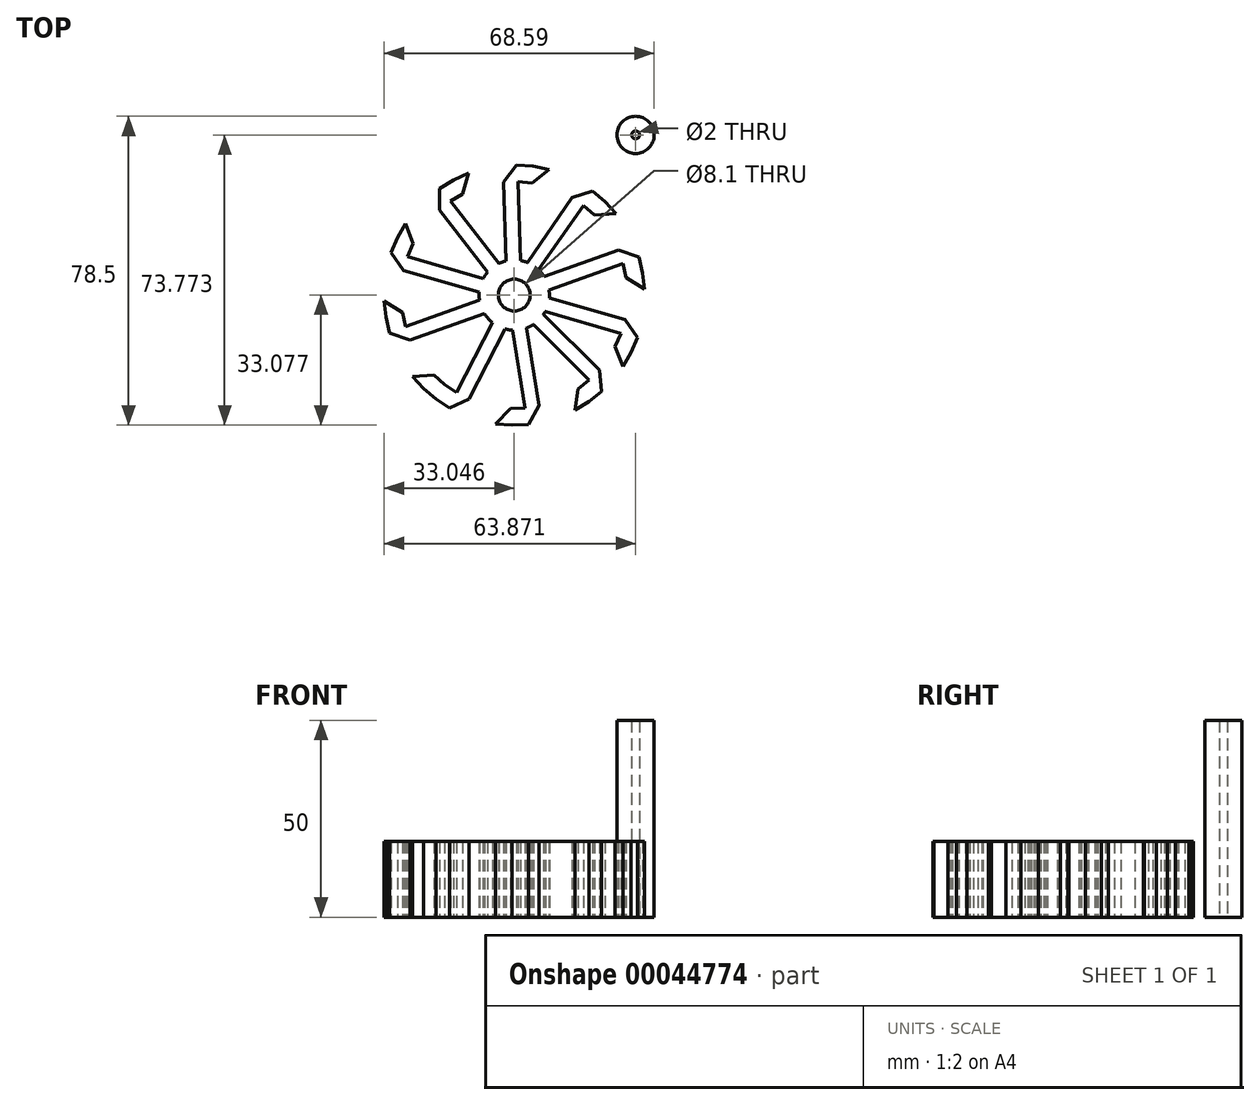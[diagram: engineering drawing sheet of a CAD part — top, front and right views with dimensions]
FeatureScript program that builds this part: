
annotation { "Feature Type Name" : "Feature", "Feature Type Description" : "" }
export const myFeature = defineFeature(function(context is Context, id is Id, definition is map)
    precondition{}
    {
        {
            var Q0;
            Q0=qCreatedBy(makeId("Top.planeOp"),FACE);
            var sketch = newSketch(context, id + "F0", { "sketchPlane" : qUnion([Q0])});
            skCircle(sketch, "E0.cCircle", {"center": v(0.32, -0.47) * mm, "radius": 28.74 * mm, "construction": true});
            skLineSegment(sketch, "E0.0", {"start": v(-15.87, 23.34) * mm, "end": v(-12.76, 25.18) * mm});
            skLineSegment(sketch, "E0.1", {"start": v(-12.76, 25.18) * mm, "end": v(-9.44, 26.62) * mm});
            skLineSegment(sketch, "E0.2", {"start": v(-9.44, 26.62) * mm, "end": v(-5.96, 27.63) * mm});
            skLineSegment(sketch, "E0.3", {"start": v(-5.96, 27.63) * mm, "end": v(-2.4, 28.2) * mm});
            skLineSegment(sketch, "E0.4", {"start": v(-2.4, 28.2) * mm, "end": v(1.22, 28.3) * mm});
            skLineSegment(sketch, "E0.5", {"start": v(1.22, 28.3) * mm, "end": v(4.82, 27.97) * mm});
            skLineSegment(sketch, "E0.6", {"start": v(4.82, 27.97) * mm, "end": v(8.35, 27.18) * mm});
            skLineSegment(sketch, "E0.7", {"start": v(8.35, 27.18) * mm, "end": v(11.75, 25.95) * mm});
            skLineSegment(sketch, "E0.8", {"start": v(11.75, 25.95) * mm, "end": v(14.98, 24.31) * mm});
            skLineSegment(sketch, "E0.9", {"start": v(14.98, 24.31) * mm, "end": v(17.97, 22.28) * mm});
            skLineSegment(sketch, "E0.10", {"start": v(17.97, 22.28) * mm, "end": v(20.68, 19.89) * mm});
            skLineSegment(sketch, "E0.11", {"start": v(20.68, 19.89) * mm, "end": v(23.07, 17.17) * mm});
            skLineSegment(sketch, "E0.12", {"start": v(23.07, 17.17) * mm, "end": v(25.1, 14.18) * mm});
            skLineSegment(sketch, "E0.13", {"start": v(25.1, 14.18) * mm, "end": v(26.74, 10.96) * mm});
            skLineSegment(sketch, "E0.14", {"start": v(26.74, 10.96) * mm, "end": v(27.97, 7.56) * mm});
            skLineSegment(sketch, "E0.15", {"start": v(27.97, 7.56) * mm, "end": v(28.76, 4.03) * mm});
            skLineSegment(sketch, "E0.16", {"start": v(28.76, 4.03) * mm, "end": v(29.1, 0.43) * mm});
            skLineSegment(sketch, "E0.17", {"start": v(29.1, 0.43) * mm, "end": v(28.98, -3.19) * mm});
            skLineSegment(sketch, "E0.18", {"start": v(28.98, -3.19) * mm, "end": v(28.42, -6.76) * mm});
            skLineSegment(sketch, "E0.19", {"start": v(28.42, -6.76) * mm, "end": v(27.4, -10.23) * mm});
            skLineSegment(sketch, "E0.20", {"start": v(27.4, -10.23) * mm, "end": v(25.97, -13.55) * mm});
            skLineSegment(sketch, "E0.21", {"start": v(25.97, -13.55) * mm, "end": v(24.13, -16.66) * mm});
            skLineSegment(sketch, "E0.22", {"start": v(24.13, -16.66) * mm, "end": v(21.91, -19.52) * mm});
            skLineSegment(sketch, "E0.23", {"start": v(21.91, -19.52) * mm, "end": v(19.36, -22.07) * mm});
            skLineSegment(sketch, "E0.24", {"start": v(19.36, -22.07) * mm, "end": v(16.5, -24.3) * mm});
            skLineSegment(sketch, "E0.25", {"start": v(16.5, -24.3) * mm, "end": v(13.39, -26.13) * mm});
            skLineSegment(sketch, "E0.26", {"start": v(13.39, -26.13) * mm, "end": v(10.07, -27.57) * mm});
            skLineSegment(sketch, "E0.27", {"start": v(10.07, -27.57) * mm, "end": v(6.6, -28.58) * mm});
            skLineSegment(sketch, "E0.28", {"start": v(6.6, -28.58) * mm, "end": v(3.02, -29.14) * mm});
            skLineSegment(sketch, "E0.29", {"start": v(3.02, -29.14) * mm, "end": v(-0.6, -29.25) * mm});
            skLineSegment(sketch, "E0.30", {"start": v(-0.6, -29.25) * mm, "end": v(-4.2, -28.91) * mm});
            skLineSegment(sketch, "E0.31", {"start": v(-4.2, -28.91) * mm, "end": v(-7.72, -28.13) * mm});
            skLineSegment(sketch, "E0.32", {"start": v(-7.72, -28.13) * mm, "end": v(-11.12, -26.9) * mm});
            skLineSegment(sketch, "E0.33", {"start": v(-11.12, -26.9) * mm, "end": v(-14.34, -25.26) * mm});
            skLineSegment(sketch, "E0.34", {"start": v(-14.34, -25.26) * mm, "end": v(-17.33, -23.23) * mm});
            skLineSegment(sketch, "E0.35", {"start": v(-17.33, -23.23) * mm, "end": v(-20.05, -20.83) * mm});
            skLineSegment(sketch, "E0.36", {"start": v(-20.05, -20.83) * mm, "end": v(-22.44, -18.12) * mm});
            skLineSegment(sketch, "E0.37", {"start": v(-22.44, -18.12) * mm, "end": v(-24.47, -15.13) * mm});
            skLineSegment(sketch, "E0.38", {"start": v(-24.47, -15.13) * mm, "end": v(-26.11, -11.9) * mm});
            skLineSegment(sketch, "E0.39", {"start": v(-26.11, -11.9) * mm, "end": v(-27.34, -8.5) * mm});
            skLineSegment(sketch, "E0.40", {"start": v(-27.34, -8.5) * mm, "end": v(-28.13, -4.98) * mm});
            skLineSegment(sketch, "E0.41", {"start": v(-28.13, -4.98) * mm, "end": v(-28.47, -1.38) * mm});
            skLineSegment(sketch, "E0.42", {"start": v(-28.47, -1.38) * mm, "end": v(-28.35, 2.24) * mm});
            skLineSegment(sketch, "E0.43", {"start": v(-28.35, 2.24) * mm, "end": v(-27.79, 5.81) * mm});
            skLineSegment(sketch, "E0.44", {"start": v(-27.79, 5.81) * mm, "end": v(-26.78, 9.28) * mm});
            skLineSegment(sketch, "E0.45", {"start": v(-26.78, 9.28) * mm, "end": v(-25.34, 12.6) * mm});
            skLineSegment(sketch, "E0.46", {"start": v(-25.34, 12.6) * mm, "end": v(-23.5, 15.71) * mm});
            skLineSegment(sketch, "E0.47", {"start": v(-23.5, 15.71) * mm, "end": v(-21.28, 18.57) * mm});
            skLineSegment(sketch, "E0.48", {"start": v(-21.28, 18.57) * mm, "end": v(-18.73, 21.13) * mm});
            skLineSegment(sketch, "E0.49", {"start": v(-18.73, 21.13) * mm, "end": v(-15.87, 23.34) * mm});
            skPoint(sketch, "E0.0.midPoint", {"position": v(-14.31, 24.26) * mm});
            skCircle(sketch, "E1.cCircle", {"center": v(0.32, -0.47) * mm, "radius": 33.02 * mm, "construction": true});
            skLineSegment(sketch, "E1.0", {"start": v(-18.67, 26.62) * mm, "end": v(-15.12, 28.79) * mm});
            skLineSegment(sketch, "E1.1", {"start": v(-15.12, 28.79) * mm, "end": v(-11.33, 30.5) * mm});
            skLineSegment(sketch, "E1.2", {"start": v(-11.33, 30.5) * mm, "end": v(-7.36, 31.7) * mm});
            skLineSegment(sketch, "E1.3", {"start": v(-7.36, 31.7) * mm, "end": v(-3.26, 32.42) * mm});
            skLineSegment(sketch, "E1.4", {"start": v(-3.26, 32.42) * mm, "end": v(0.89, 32.6) * mm});
            skLineSegment(sketch, "E1.5", {"start": v(0.89, 32.6) * mm, "end": v(5.03, 32.27) * mm});
            skLineSegment(sketch, "E1.6", {"start": v(5.03, 32.27) * mm, "end": v(9.1, 31.42) * mm});
            skLineSegment(sketch, "E1.7", {"start": v(9.1, 31.42) * mm, "end": v(13.02, 30.07) * mm});
            skLineSegment(sketch, "E1.8", {"start": v(13.02, 30.07) * mm, "end": v(16.75, 28.24) * mm});
            skLineSegment(sketch, "E1.9", {"start": v(16.75, 28.24) * mm, "end": v(20.22, 25.95) * mm});
            skLineSegment(sketch, "E1.10", {"start": v(20.22, 25.95) * mm, "end": v(23.38, 23.25) * mm});
            skLineSegment(sketch, "E1.11", {"start": v(23.38, 23.25) * mm, "end": v(26.17, 20.17) * mm});
            skLineSegment(sketch, "E1.12", {"start": v(26.17, 20.17) * mm, "end": v(28.55, 16.77) * mm});
            skLineSegment(sketch, "E1.13", {"start": v(28.55, 16.77) * mm, "end": v(30.49, 13.1) * mm});
            skLineSegment(sketch, "E1.14", {"start": v(30.49, 13.1) * mm, "end": v(31.95, 9.2) * mm});
            skLineSegment(sketch, "E1.15", {"start": v(31.95, 9.2) * mm, "end": v(32.92, 5.16) * mm});
            skLineSegment(sketch, "E1.16", {"start": v(32.92, 5.16) * mm, "end": v(33.37, 1.03) * mm});
            skLineSegment(sketch, "E1.17", {"start": v(33.37, 1.03) * mm, "end": v(33.3, -3.12) * mm});
            skLineSegment(sketch, "E1.18", {"start": v(33.3, -3.12) * mm, "end": v(32.7, -7.23) * mm});
            skLineSegment(sketch, "E1.19", {"start": v(32.7, -7.23) * mm, "end": v(31.6, -11.24) * mm});
            skLineSegment(sketch, "E1.20", {"start": v(31.6, -11.24) * mm, "end": v(30, -15.07) * mm});
            skLineSegment(sketch, "E1.21", {"start": v(30, -15.07) * mm, "end": v(27.94, -18.68) * mm});
            skLineSegment(sketch, "E1.22", {"start": v(27.94, -18.68) * mm, "end": v(25.44, -22) * mm});
            skLineSegment(sketch, "E1.23", {"start": v(25.44, -22) * mm, "end": v(22.54, -24.98) * mm});
            skLineSegment(sketch, "E1.24", {"start": v(22.54, -24.98) * mm, "end": v(19.3, -27.57) * mm});
            skLineSegment(sketch, "E1.25", {"start": v(19.3, -27.57) * mm, "end": v(15.75, -29.74) * mm});
            skLineSegment(sketch, "E1.26", {"start": v(15.75, -29.74) * mm, "end": v(11.96, -31.44) * mm});
            skLineSegment(sketch, "E1.27", {"start": v(11.96, -31.44) * mm, "end": v(7.99, -32.65) * mm});
            skLineSegment(sketch, "E1.28", {"start": v(7.99, -32.65) * mm, "end": v(3.9, -33.36) * mm});
            skLineSegment(sketch, "E1.29", {"start": v(3.9, -33.36) * mm, "end": v(-0.25, -33.55) * mm});
            skLineSegment(sketch, "E1.30", {"start": v(-0.25, -33.55) * mm, "end": v(-4.4, -33.22) * mm});
            skLineSegment(sketch, "E1.31", {"start": v(-4.4, -33.22) * mm, "end": v(-8.46, -32.37) * mm});
            skLineSegment(sketch, "E1.32", {"start": v(-8.46, -32.37) * mm, "end": v(-12.4, -31.02) * mm});
            skLineSegment(sketch, "E1.33", {"start": v(-12.4, -31.02) * mm, "end": v(-16.12, -29.19) * mm});
            skLineSegment(sketch, "E1.34", {"start": v(-16.12, -29.19) * mm, "end": v(-19.59, -26.9) * mm});
            skLineSegment(sketch, "E1.35", {"start": v(-19.59, -26.9) * mm, "end": v(-22.74, -24.2) * mm});
            skLineSegment(sketch, "E1.36", {"start": v(-22.74, -24.2) * mm, "end": v(-25.54, -21.12) * mm});
            skLineSegment(sketch, "E1.37", {"start": v(-25.54, -21.12) * mm, "end": v(-27.92, -17.72) * mm});
            skLineSegment(sketch, "E1.38", {"start": v(-27.92, -17.72) * mm, "end": v(-29.86, -14.04) * mm});
            skLineSegment(sketch, "E1.39", {"start": v(-29.86, -14.04) * mm, "end": v(-31.32, -10.15) * mm});
            skLineSegment(sketch, "E1.40", {"start": v(-31.32, -10.15) * mm, "end": v(-32.28, -6.11) * mm});
            skLineSegment(sketch, "E1.41", {"start": v(-32.28, -6.11) * mm, "end": v(-32.73, -1.98) * mm});
            skLineSegment(sketch, "E1.42", {"start": v(-32.73, -1.98) * mm, "end": v(-32.66, 2.17) * mm});
            skLineSegment(sketch, "E1.43", {"start": v(-32.66, 2.17) * mm, "end": v(-32.07, 6.29) * mm});
            skLineSegment(sketch, "E1.44", {"start": v(-32.07, 6.29) * mm, "end": v(-30.97, 10.3) * mm});
            skLineSegment(sketch, "E1.45", {"start": v(-30.97, 10.3) * mm, "end": v(-29.37, 14.13) * mm});
            skLineSegment(sketch, "E1.46", {"start": v(-29.37, 14.13) * mm, "end": v(-27.3, 17.73) * mm});
            skLineSegment(sketch, "E1.47", {"start": v(-27.3, 17.73) * mm, "end": v(-24.8, 21.05) * mm});
            skLineSegment(sketch, "E1.48", {"start": v(-24.8, 21.05) * mm, "end": v(-21.91, 24.03) * mm});
            skLineSegment(sketch, "E1.49", {"start": v(-21.91, 24.03) * mm, "end": v(-18.67, 26.62) * mm});
            skPoint(sketch, "E1.0.midPoint", {"position": v(-16.9, 27.7) * mm});
            skCircle(sketch, "E2", {"center": v(0.32, -0.47) * mm, "radius": 8.92 * mm});
            skCircle(sketch, "E3", {"center": v(0.32, -0.47) * mm, "radius": 4.72 * mm});
            skLineSegment(sketch, "E4", {"start": v(0.89, 32.6) * mm, "end": v(-2.4, 28.2) * mm});
            skLineSegment(sketch, "E5", {"start": v(9.1, 31.42) * mm, "end": v(4.82, 27.97) * mm});
            skLineSegment(sketch, "E6", {"start": v(14.98, 24.31) * mm, "end": v(20.22, 25.95) * mm});
            skLineSegment(sketch, "E7", {"start": v(26.17, 20.17) * mm, "end": v(20.68, 19.89) * mm});
            skLineSegment(sketch, "E8", {"start": v(26.74, 10.96) * mm, "end": v(31.95, 9.2) * mm});
            skLineSegment(sketch, "E9", {"start": v(33.37, 1.03) * mm, "end": v(28.76, 4.03) * mm});
            skLineSegment(sketch, "E10", {"start": v(14.98, 24.31) * mm, "end": v(3.73, 7.77) * mm});
            skLineSegment(sketch, "E11", {"start": v(17.97, 22.3) * mm, "end": v(6.5, 5.96) * mm});
            skLineSegment(sketch, "E12", {"start": v(-2.4, 28.2) * mm, "end": v(-1.77, 8.2) * mm});
            skLineSegment(sketch, "E13", {"start": v(1.22, 28.3) * mm, "end": v(1.85, 8.32) * mm});
            skLineSegment(sketch, "E14", {"start": v(26.74, 10.96) * mm, "end": v(7.93, 4.19) * mm});
            skLineSegment(sketch, "E15", {"start": v(27.97, 7.56) * mm, "end": v(9.15, 0.78) * mm});
            skLineSegment(sketch, "E16", {"start": v(28.42, -6.76) * mm, "end": v(31.6, -11.24) * mm});
            skLineSegment(sketch, "E17", {"start": v(27.94, -18.68) * mm, "end": v(25.97, -13.55) * mm});
            skLineSegment(sketch, "E18", {"start": v(28.42, -6.76) * mm, "end": v(9.21, -1.18) * mm});
            skLineSegment(sketch, "E19", {"start": v(27.4, -10.23) * mm, "end": v(8.2, -4.65) * mm});
            skLineSegment(sketch, "E20", {"start": v(21.91, -19.52) * mm, "end": v(7.77, -5.37) * mm});
            skLineSegment(sketch, "E21", {"start": v(19.36, -22.07) * mm, "end": v(5.22, -7.93) * mm});
            skLineSegment(sketch, "E22", {"start": v(21.91, -19.52) * mm, "end": v(22.54, -24.98) * mm});
            skLineSegment(sketch, "E23", {"start": v(16.5, -24.3) * mm, "end": v(15.75, -29.74) * mm});
            skLineSegment(sketch, "E24", {"start": v(-11.33, 30.5) * mm, "end": v(-12.76, 25.18) * mm});
            skLineSegment(sketch, "E25", {"start": v(-18.67, 26.62) * mm, "end": v(-18.73, 21.13) * mm});
            skLineSegment(sketch, "E26", {"start": v(-15.87, 23.34) * mm, "end": v(-3.61, 7.54) * mm});
            skLineSegment(sketch, "E27", {"start": v(-18.73, 21.13) * mm, "end": v(-6.47, 5.32) * mm});
            skLineSegment(sketch, "E28", {"start": v(6.6, -28.58) * mm, "end": v(3.9, -33.36) * mm});
            skLineSegment(sketch, "E29", {"start": v(-0.6, -29.25) * mm, "end": v(-4.4, -33.22) * mm});
            skLineSegment(sketch, "E30", {"start": v(3.02, -29.14) * mm, "end": v(-0.1, -9.39) * mm});
            skLineSegment(sketch, "E31", {"start": v(6.6, -28.58) * mm, "end": v(3.47, -8.82) * mm});
            skLineSegment(sketch, "E32", {"start": v(-27.3, 17.73) * mm, "end": v(-25.34, 12.6) * mm});
            skLineSegment(sketch, "E33", {"start": v(-30.97, 10.3) * mm, "end": v(-27.79, 5.81) * mm});
            skLineSegment(sketch, "E34", {"start": v(-27.79, 5.81) * mm, "end": v(-8.58, 0.23) * mm});
            skLineSegment(sketch, "E35", {"start": v(-26.78, 9.28) * mm, "end": v(-7.57, 3.7) * mm});
            skLineSegment(sketch, "E36", {"start": v(-32.73, -1.98) * mm, "end": v(-28.13, -4.98) * mm});
            skLineSegment(sketch, "E37", {"start": v(-31.32, -10.15) * mm, "end": v(-26.11, -11.9) * mm});
            skLineSegment(sketch, "E38", {"start": v(-26.11, -11.9) * mm, "end": v(-7.3, -5.13) * mm});
            skLineSegment(sketch, "E39", {"start": v(-27.34, -8.5) * mm, "end": v(-8.52, -1.73) * mm});
            skLineSegment(sketch, "E40", {"start": v(-25.54, -21.12) * mm, "end": v(-20.05, -20.83) * mm});
            skLineSegment(sketch, "E41", {"start": v(-16.12, -29.19) * mm, "end": v(-11.12, -26.9) * mm});
            skLineSegment(sketch, "E42", {"start": v(-11.12, -26.9) * mm, "end": v(-2.04, -9.08) * mm});
            skLineSegment(sketch, "E43", {"start": v(-14.34, -25.26) * mm, "end": v(-5.26, -7.44) * mm});
            skCircle(sketch, "E44", {"center": v(31.14, 40.22) * mm, "radius": 4.72 * mm});
            skCircle(sketch, "E45", {"center": v(31.14, 40.22) * mm, "radius": 1 * mm});
            skSolve(sketch);
        }
        {
            var Q0;
            Q0=makeQuery(id+"F0.imprint","IMPRINT",FACE,{"disambiguationData":[TD([[makeQuery(id+"F0.imprint","IMPRINT",EDGE,{"derivedFrom":sQuery(id+"F0.wireOp",EDGE,"E0.49")}),-1.0]])]});
            var Q1;
            Q1=makeQuery(id+"F0.imprint","IMPRINT",FACE,{"disambiguationData":[TD([[makeQuery(id+"F0.imprint","IMPRINT",EDGE,{"derivedFrom":sQuery(id+"F0.wireOp",EDGE,"E0.4")}),-1.0]])]});
            var Q2;
            {var subQ5=sQuery(id+"F0.wireOp",EDGE,"E10");Q2=makeQuery(id+"F0.imprint","IMPRINT",FACE,{"disambiguationData":[TD([[makeQuery(id+"F0.imprint","IMPRINT",EDGE,{"derivedFrom":subQ5}),1.0]])]});}
            var Q3;
            Q3=makeQuery(id+"F0.imprint","IMPRINT",FACE,{"disambiguationData":[TD([[makeQuery(id+"F0.imprint","IMPRINT",EDGE,{"derivedFrom":sQuery(id+"F0.wireOp",EDGE,"E0.14")}),-1.0]])]});
            var Q4;
            Q4=makeQuery(id+"F0.imprint","IMPRINT",FACE,{"disambiguationData":[TD([[makeQuery(id+"F0.imprint","IMPRINT",EDGE,{"derivedFrom":sQuery(id+"F0.wireOp",EDGE,"E0.19")}),-1.0]])]});
            var Q5;
            Q5=makeQuery(id+"F0.imprint","IMPRINT",FACE,{"disambiguationData":[TD([[makeQuery(id+"F0.imprint","IMPRINT",EDGE,{"derivedFrom":sQuery(id+"F0.wireOp",EDGE,"E0.23")}),-1.0]])]});
            var Q6;
            Q6=makeQuery(id+"F0.imprint","IMPRINT",FACE,{"disambiguationData":[TD([[makeQuery(id+"F0.imprint","IMPRINT",EDGE,{"derivedFrom":sQuery(id+"F0.wireOp",EDGE,"E0.28")}),-1.0]])]});
            var Q7;
            Q7=makeQuery(id+"F0.imprint","IMPRINT",FACE,{"disambiguationData":[TD([[makeQuery(id+"F0.imprint","IMPRINT",EDGE,{"derivedFrom":sQuery(id+"F0.wireOp",EDGE,"E0.33")}),-1.0]])]});
            var Q8;
            Q8=makeQuery(id+"F0.imprint","IMPRINT",FACE,{"disambiguationData":[TD([[makeQuery(id+"F0.imprint","IMPRINT",EDGE,{"derivedFrom":sQuery(id+"F0.wireOp",EDGE,"E0.39")}),-1.0]])]});
            var Q9;
            Q9=makeQuery(id+"F0.imprint","IMPRINT",FACE,{"disambiguationData":[TD([[makeQuery(id+"F0.imprint","IMPRINT",EDGE,{"derivedFrom":sQuery(id+"F0.wireOp",EDGE,"E0.44")}),-1.0]])]});
            var Q10;
            Q10=makeQuery(id+"F0.imprint","IMPRINT",FACE,{"disambiguationData":[TD([[makeQuery(id+"F0.imprint","IMPRINT",EDGE,{"derivedFrom":sQuery(id+"F0.wireOp",EDGE,"E3")}),-1.0]])]});
            var Q11;
            Q11=makeQuery(id+"F0.imprint","IMPRINT",FACE,{"disambiguationData":[TD([[makeQuery(id+"F0.imprint","IMPRINT",EDGE,{"derivedFrom":sQuery(id+"F0.wireOp",EDGE,"E3")}),1.0]])]});
            var Q12;
            Q12=makeQuery(id+"F0.imprint","IMPRINT",FACE,{"disambiguationData":[TD([[makeQuery(id+"F0.imprint","IMPRINT",EDGE,{"derivedFrom":sQuery(id+"F0.wireOp",EDGE,"E0.44")}),1.0]])]});
            var Q13;
            Q13=makeQuery(id+"F0.imprint","IMPRINT",FACE,{"disambiguationData":[TD([[makeQuery(id+"F0.imprint","IMPRINT",EDGE,{"derivedFrom":sQuery(id+"F0.wireOp",EDGE,"E0.39")}),1.0]])]});
            var Q14;
            Q14=makeQuery(id+"F0.imprint","IMPRINT",FACE,{"disambiguationData":[TD([[makeQuery(id+"F0.imprint","IMPRINT",EDGE,{"derivedFrom":sQuery(id+"F0.wireOp",EDGE,"E0.33")}),1.0]])]});
            var Q15;
            Q15=makeQuery(id+"F0.imprint","IMPRINT",FACE,{"disambiguationData":[TD([[makeQuery(id+"F0.imprint","IMPRINT",EDGE,{"derivedFrom":sQuery(id+"F0.wireOp",EDGE,"E0.28")}),1.0]])]});
            var Q16;
            Q16=makeQuery(id+"F0.imprint","IMPRINT",FACE,{"disambiguationData":[TD([[makeQuery(id+"F0.imprint","IMPRINT",EDGE,{"derivedFrom":sQuery(id+"F0.wireOp",EDGE,"E0.23")}),1.0]])]});
            var Q17;
            Q17=makeQuery(id+"F0.imprint","IMPRINT",FACE,{"disambiguationData":[TD([[makeQuery(id+"F0.imprint","IMPRINT",EDGE,{"derivedFrom":sQuery(id+"F0.wireOp",EDGE,"E0.19")}),1.0]])]});
            var Q18;
            Q18=makeQuery(id+"F0.imprint","IMPRINT",FACE,{"disambiguationData":[TD([[makeQuery(id+"F0.imprint","IMPRINT",EDGE,{"derivedFrom":sQuery(id+"F0.wireOp",EDGE,"E0.14")}),1.0]])]});
            var Q19;
            {var subQ3=sQuery(id+"F0.wireOp",EDGE,"E0.10");Q19=makeQuery(id+"F0.imprint","IMPRINT",FACE,{"disambiguationData":[TD([[makeQuery(id+"F0.imprint","IMPRINT",EDGE,{"derivedFrom":subQ3}),1.0]])]});}
            var Q20;
            Q20=makeQuery(id+"F0.imprint","IMPRINT",FACE,{"disambiguationData":[TD([[makeQuery(id+"F0.imprint","IMPRINT",EDGE,{"derivedFrom":sQuery(id+"F0.wireOp",EDGE,"E0.4")}),1.0]])]});
            var Q21;
            Q21=makeQuery(id+"F0.imprint","IMPRINT",FACE,{"disambiguationData":[TD([[makeQuery(id+"F0.imprint","IMPRINT",EDGE,{"derivedFrom":sQuery(id+"F0.wireOp",EDGE,"E0.0")}),1.0]])]});
            extrude(context, id + "F1", {"entities" : qUnion([Q0, Q1, Q2, Q3, Q4, Q5, Q6, Q7, Q8, Q9, Q10, Q11, Q12, Q13, Q14, Q15, Q16, Q17, Q18, Q19, Q20, Q21]), "depth" : 19.22 * mm});
        }
        {
            var Q0;
            Q0=qCreatedBy(makeId("Top.planeOp"),FACE);
            var sketch = newSketch(context, id + "F2", { "sketchPlane" : qUnion([Q0])});
            skCircle(sketch, "E46", {"center": v(0.32, -0.47) * mm, "radius": 1.5 * mm});
            skSolve(sketch);
        }
        {
            var Q0;
            Q0=sQuery(id+"F2.wireOp",VERTEX,"E46.center");
            var Q1;
            Q1=makeQuery(id+"F1.opExtrude","SWEPT_BODY",BODY,{"disambiguationData":[OSD([sQuery(id+"F0.wireOp",EDGE,"E0.0"),sQuery(id+"F0.wireOp",EDGE,"E0.5"),sQuery(id+"F0.wireOp",EDGE,"E0.9"),sQuery(id+"F0.wireOp",EDGE,"E0.10"),sQuery(id+"F0.wireOp",EDGE,"E0.15"),sQuery(id+"F0.wireOp",EDGE,"E0.20"),sQuery(id+"F0.wireOp",EDGE,"E0.24"),sQuery(id+"F0.wireOp",EDGE,"E0.29"),sQuery(id+"F0.wireOp",EDGE,"E0.34"),sQuery(id+"F0.wireOp",EDGE,"E0.35"),sQuery(id+"F0.wireOp",EDGE,"E0.40"),sQuery(id+"F0.wireOp",EDGE,"E0.45"),sQuery(id+"F0.wireOp",EDGE,"E1.0"),sQuery(id+"F0.wireOp",EDGE,"E1.1"),sQuery(id+"F0.wireOp",EDGE,"E1.5"),sQuery(id+"F0.wireOp",EDGE,"E1.6"),sQuery(id+"F0.wireOp",EDGE,"E1.10"),sQuery(id+"F0.wireOp",EDGE,"E1.11"),sQuery(id+"F0.wireOp",EDGE,"E1.15"),sQuery(id+"F0.wireOp",EDGE,"E1.16"),sQuery(id+"F0.wireOp",EDGE,"E1.20"),sQuery(id+"F0.wireOp",EDGE,"E1.21"),sQuery(id+"F0.wireOp",EDGE,"E1.24"),sQuery(id+"F0.wireOp",EDGE,"E1.25"),sQuery(id+"F0.wireOp",EDGE,"E1.29"),sQuery(id+"F0.wireOp",EDGE,"E1.30"),sQuery(id+"F0.wireOp",EDGE,"E1.34"),sQuery(id+"F0.wireOp",EDGE,"E1.35"),sQuery(id+"F0.wireOp",EDGE,"E1.36"),sQuery(id+"F0.wireOp",EDGE,"E1.40"),sQuery(id+"F0.wireOp",EDGE,"E1.41"),sQuery(id+"F0.wireOp",EDGE,"E1.45"),sQuery(id+"F0.wireOp",EDGE,"E1.46"),sQuery(id+"F0.wireOp",EDGE,"E2"),sQuery(id+"F0.wireOp",EDGE,"E4"),sQuery(id+"F0.wireOp",EDGE,"E5"),sQuery(id+"F0.wireOp",EDGE,"E6"),sQuery(id+"F0.wireOp",EDGE,"E7"),sQuery(id+"F0.wireOp",EDGE,"E8"),sQuery(id+"F0.wireOp",EDGE,"E9"),sQuery(id+"F0.wireOp",EDGE,"E10"),sQuery(id+"F0.wireOp",EDGE,"E11"),sQuery(id+"F0.wireOp",EDGE,"E12"),sQuery(id+"F0.wireOp",EDGE,"E13"),sQuery(id+"F0.wireOp",EDGE,"E14"),sQuery(id+"F0.wireOp",EDGE,"E15"),sQuery(id+"F0.wireOp",EDGE,"E16"),sQuery(id+"F0.wireOp",EDGE,"E17"),sQuery(id+"F0.wireOp",EDGE,"E18"),sQuery(id+"F0.wireOp",EDGE,"E19"),sQuery(id+"F0.wireOp",EDGE,"E20"),sQuery(id+"F0.wireOp",EDGE,"E21"),sQuery(id+"F0.wireOp",EDGE,"E22"),sQuery(id+"F0.wireOp",EDGE,"E23"),sQuery(id+"F0.wireOp",EDGE,"E24"),sQuery(id+"F0.wireOp",EDGE,"E25"),sQuery(id+"F0.wireOp",EDGE,"E26"),sQuery(id+"F0.wireOp",EDGE,"E27"),sQuery(id+"F0.wireOp",EDGE,"E28"),sQuery(id+"F0.wireOp",EDGE,"E29"),sQuery(id+"F0.wireOp",EDGE,"E30"),sQuery(id+"F0.wireOp",EDGE,"E31"),sQuery(id+"F0.wireOp",EDGE,"E32"),sQuery(id+"F0.wireOp",EDGE,"E33"),sQuery(id+"F0.wireOp",EDGE,"E34"),sQuery(id+"F0.wireOp",EDGE,"E35"),sQuery(id+"F0.wireOp",EDGE,"E36"),sQuery(id+"F0.wireOp",EDGE,"E37"),sQuery(id+"F0.wireOp",EDGE,"E38"),sQuery(id+"F0.wireOp",EDGE,"E39"),sQuery(id+"F0.wireOp",EDGE,"E40"),sQuery(id+"F0.wireOp",EDGE,"E41"),sQuery(id+"F0.wireOp",EDGE,"E42"),sQuery(id+"F0.wireOp",EDGE,"E43")])]});
            hole(context, id + "F3", {"style" : HoleStyle.SIMPLE, "holeDiameter" : 8.1 * mm, "endStyle" : HoleEndStyle.THROUGH, "oppositeDirection" : true, "locations" : qUnion([Q0]), "scope" : qUnion([Q1])});
        }
        {
            var Q0;
            Q0=makeQuery(id+"F1.opExtrude","CAP_FACE",FACE,{"disambiguationData":[OSD([sQuery(id+"F0.wireOp",EDGE,"E0.0"),sQuery(id+"F0.wireOp",EDGE,"E0.5"),sQuery(id+"F0.wireOp",EDGE,"E0.9"),sQuery(id+"F0.wireOp",EDGE,"E0.10"),sQuery(id+"F0.wireOp",EDGE,"E0.15"),sQuery(id+"F0.wireOp",EDGE,"E0.20"),sQuery(id+"F0.wireOp",EDGE,"E0.24"),sQuery(id+"F0.wireOp",EDGE,"E0.29"),sQuery(id+"F0.wireOp",EDGE,"E0.34"),sQuery(id+"F0.wireOp",EDGE,"E0.35"),sQuery(id+"F0.wireOp",EDGE,"E0.40"),sQuery(id+"F0.wireOp",EDGE,"E0.45"),sQuery(id+"F0.wireOp",EDGE,"E1.0"),sQuery(id+"F0.wireOp",EDGE,"E1.1"),sQuery(id+"F0.wireOp",EDGE,"E1.5"),sQuery(id+"F0.wireOp",EDGE,"E1.6"),sQuery(id+"F0.wireOp",EDGE,"E1.10"),sQuery(id+"F0.wireOp",EDGE,"E1.11"),sQuery(id+"F0.wireOp",EDGE,"E1.15"),sQuery(id+"F0.wireOp",EDGE,"E1.16"),sQuery(id+"F0.wireOp",EDGE,"E1.20"),sQuery(id+"F0.wireOp",EDGE,"E1.21"),sQuery(id+"F0.wireOp",EDGE,"E1.24"),sQuery(id+"F0.wireOp",EDGE,"E1.25"),sQuery(id+"F0.wireOp",EDGE,"E1.29"),sQuery(id+"F0.wireOp",EDGE,"E1.30"),sQuery(id+"F0.wireOp",EDGE,"E1.34"),sQuery(id+"F0.wireOp",EDGE,"E1.35"),sQuery(id+"F0.wireOp",EDGE,"E1.36"),sQuery(id+"F0.wireOp",EDGE,"E1.40"),sQuery(id+"F0.wireOp",EDGE,"E1.41"),sQuery(id+"F0.wireOp",EDGE,"E1.45"),sQuery(id+"F0.wireOp",EDGE,"E1.46"),sQuery(id+"F0.wireOp",EDGE,"E2"),sQuery(id+"F0.wireOp",EDGE,"E4"),sQuery(id+"F0.wireOp",EDGE,"E5"),sQuery(id+"F0.wireOp",EDGE,"E6"),sQuery(id+"F0.wireOp",EDGE,"E7"),sQuery(id+"F0.wireOp",EDGE,"E8"),sQuery(id+"F0.wireOp",EDGE,"E9"),sQuery(id+"F0.wireOp",EDGE,"E10"),sQuery(id+"F0.wireOp",EDGE,"E11"),sQuery(id+"F0.wireOp",EDGE,"E12"),sQuery(id+"F0.wireOp",EDGE,"E13"),sQuery(id+"F0.wireOp",EDGE,"E14"),sQuery(id+"F0.wireOp",EDGE,"E15"),sQuery(id+"F0.wireOp",EDGE,"E16"),sQuery(id+"F0.wireOp",EDGE,"E17"),sQuery(id+"F0.wireOp",EDGE,"E18"),sQuery(id+"F0.wireOp",EDGE,"E19"),sQuery(id+"F0.wireOp",EDGE,"E20"),sQuery(id+"F0.wireOp",EDGE,"E21"),sQuery(id+"F0.wireOp",EDGE,"E22"),sQuery(id+"F0.wireOp",EDGE,"E23"),sQuery(id+"F0.wireOp",EDGE,"E24"),sQuery(id+"F0.wireOp",EDGE,"E25"),sQuery(id+"F0.wireOp",EDGE,"E26"),sQuery(id+"F0.wireOp",EDGE,"E27"),sQuery(id+"F0.wireOp",EDGE,"E28"),sQuery(id+"F0.wireOp",EDGE,"E29"),sQuery(id+"F0.wireOp",EDGE,"E30"),sQuery(id+"F0.wireOp",EDGE,"E31"),sQuery(id+"F0.wireOp",EDGE,"E32"),sQuery(id+"F0.wireOp",EDGE,"E33"),sQuery(id+"F0.wireOp",EDGE,"E34"),sQuery(id+"F0.wireOp",EDGE,"E35"),sQuery(id+"F0.wireOp",EDGE,"E36"),sQuery(id+"F0.wireOp",EDGE,"E37"),sQuery(id+"F0.wireOp",EDGE,"E38"),sQuery(id+"F0.wireOp",EDGE,"E39"),sQuery(id+"F0.wireOp",EDGE,"E40"),sQuery(id+"F0.wireOp",EDGE,"E41"),sQuery(id+"F0.wireOp",EDGE,"E42"),sQuery(id+"F0.wireOp",EDGE,"E43")])],"isStart":false});
            var sketch = newSketch(context, id + "F4", { "sketchPlane" : qUnion([Q0])});
            skSolve(sketch);
        }
        {
            var Q0;
            Q0=makeQuery(id+"F0.imprint","IMPRINT",FACE,{"disambiguationData":[TD([[makeQuery(id+"F0.imprint","IMPRINT",EDGE,{"derivedFrom":sQuery(id+"F0.wireOp",EDGE,"E44")}),1.0]])]});
            extrude(context, id + "F5", {"entities" : qUnion([Q0]), "depth" : 50 * mm});
        }
    });
